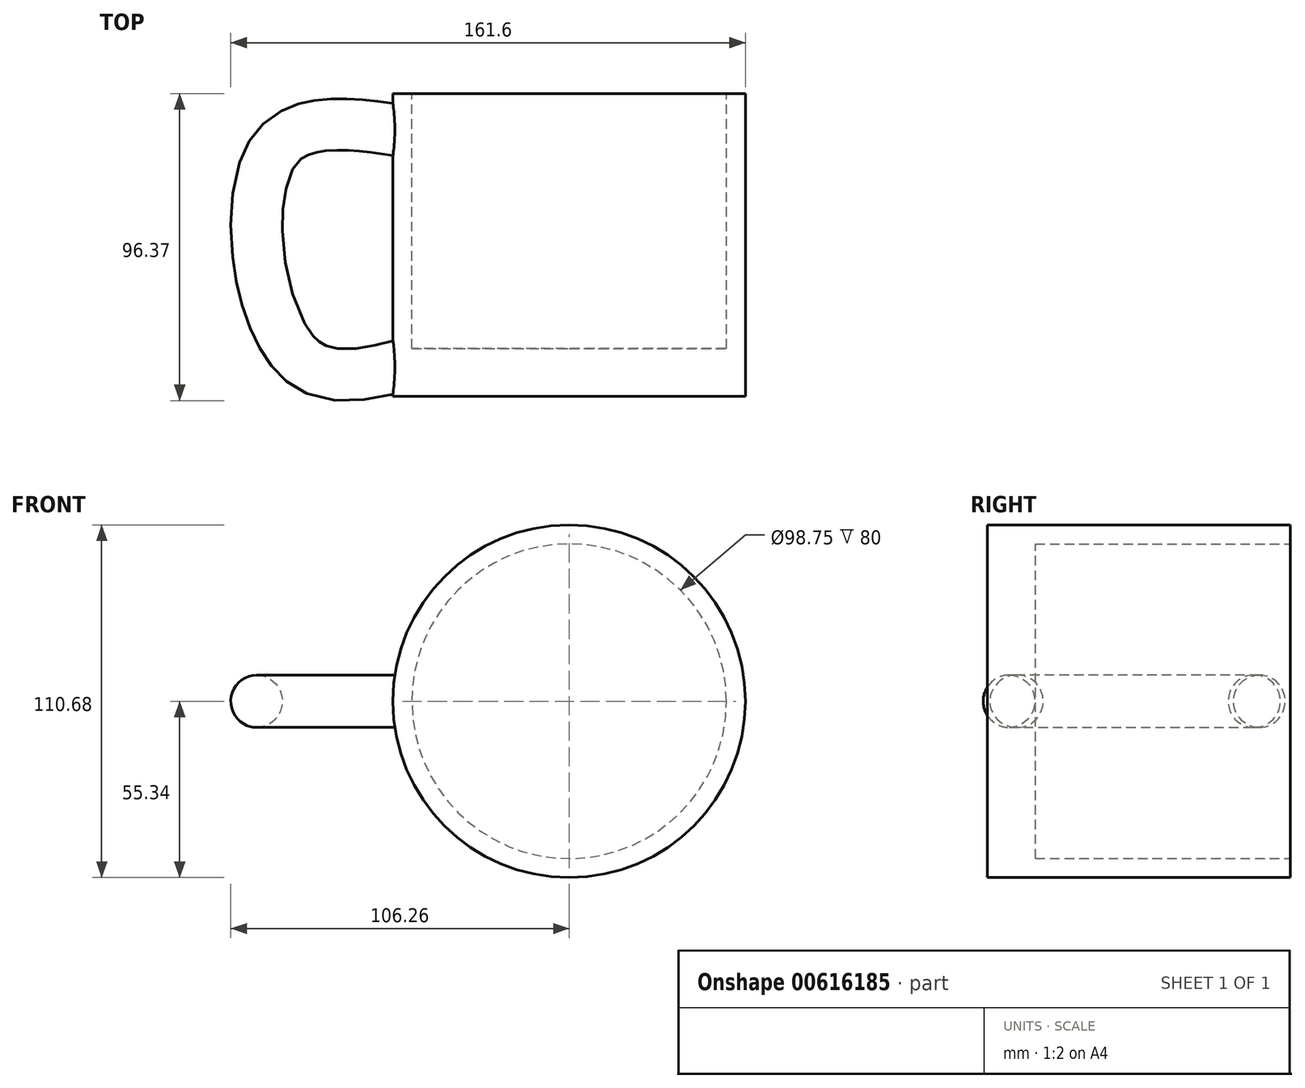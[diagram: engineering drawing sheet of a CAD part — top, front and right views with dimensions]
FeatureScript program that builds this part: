
annotation { "Feature Type Name" : "Feature", "Feature Type Description" : "" }
export const myFeature = defineFeature(function(context is Context, id is Id, definition is map)
    precondition{}
    {
        {
            var Q0;
            Q0=qCreatedBy(makeId("Front.planeOp"),FACE);
            var sketch = newSketch(context, id + "F0", { "sketchPlane" : qUnion([Q0])});
            skCircle(sketch, "E0", {"center": v(0, 0) * mm, "radius": 55.34 * mm});
            skSolve(sketch);
        }
        {
            var Q0;
            Q0=makeQuery(id+"F0.imprint","IMPRINT",FACE,{"disambiguationData":[TD([[makeQuery(id+"F0.imprint","IMPRINT",EDGE,{"derivedFrom":sQuery(id+"F0.wireOp",EDGE,"E0")}),1.0]])]});
            extrude(context, id + "F1", {"entities" : qUnion([Q0]), "depth" : 95 * mm, "offsetDistance" : 25 * mm});
        }
        {
            var Q0;
            Q0=qCreatedBy(makeId("Top.planeOp"),FACE);
            var sketch = newSketch(context, id + "F2", { "sketchPlane" : qUnion([Q0])});
            skFitSpline(sketch, "E1", {"points": [v(-44.13, -84.17) * mm, v(-86.38, -83.46) * mm, v(-94.1, -17.43) * mm, v(-46.46, -11.23) * mm], "startDerivative": vector(-158.08, -49.09) * mm, "endDerivative": vector(182.04, -31.26) * mm});
            skSolve(sketch);
        }
        {
            var Q0;
            Q0=qCreatedBy(makeId("Right.planeOp"),FACE);
            cPlane(context, id + "F3", {"entities" : qUnion([Q0]), "cplaneType" : CPlaneType.OFFSET, "offset" : 49 * mm, "oppositeDirection" : true, "width" : 150 * mm, "height" : 150 * mm});
        }
        {
            var Q0;
            Q0=qCreatedBy(id+"F3.planeOp",FACE);
            var sketch = newSketch(context, id + "F4", { "sketchPlane" : qUnion([Q0])});
            skCircle(sketch, "E2", {"center": v(-12.3, 0) * mm, "radius": 8.22 * mm});
            skSolve(sketch);
        }
        {
            var Q0;
            Q0 = qSketchRegion(id + "F4", true);
            var Q1;
            Q1=sQuery(id+"F2.wireOp",EDGE,"E1");
            sweep(context, id + "F5", {"operationType" : NewBodyOperationType.ADD, "profiles" : qUnion([Q0]), "path" : qUnion([Q1])});
        }
        {
            var Q0;
            Q0=qCreatedBy(makeId("Front.planeOp"),FACE);
            var sketch = newSketch(context, id + "F6", { "sketchPlane" : qUnion([Q0])});
            skCircle(sketch, "E3", {"center": v(0, 0) * mm, "radius": 49.38 * mm});
            skSolve(sketch);
        }
        {
            var Q0;
            Q0 = qSketchRegion(id + "F6", true);
            extrude(context, id + "F7", {"entities" : qUnion([Q0]), "operationType" : NewBodyOperationType.REMOVE, "depth" : 80 * mm, "offsetDistance" : 25 * mm});
        }
    });
